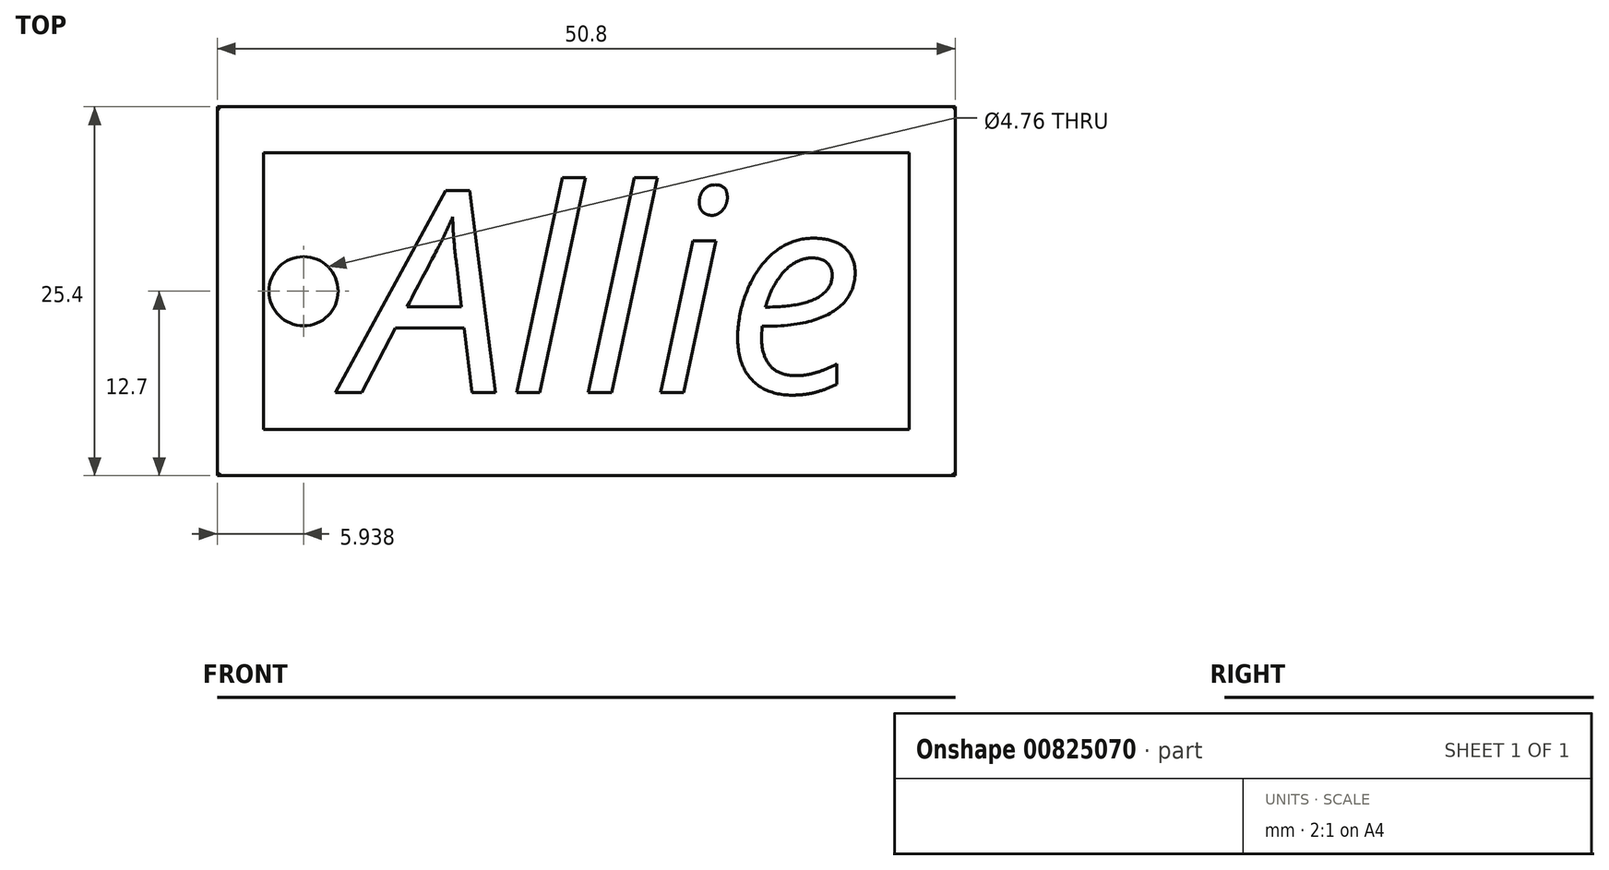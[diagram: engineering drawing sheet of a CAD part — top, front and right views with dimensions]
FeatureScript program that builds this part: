
annotation { "Feature Type Name" : "Feature", "Feature Type Description" : "" }
export const myFeature = defineFeature(function(context is Context, id is Id, definition is map)
    precondition{}
    {
        {
            var Q0;
            Q0=qCreatedBy(makeId("Top.planeOp"),FACE);
            var sketch = newSketch(context, id + "F0", { "sketchPlane" : qUnion([Q0])});
            skLineSegment(sketch, "E0.bottom", {"start": v(0, 0) * mm, "end": v(50.8, 0) * mm});
            skLineSegment(sketch, "E0.top", {"start": v(0, 25.4) * mm, "end": v(50.8, 25.4) * mm});
            skLineSegment(sketch, "E0.left", {"start": v(0, 0) * mm, "end": v(0, 25.4) * mm});
            skLineSegment(sketch, "E0.right", {"start": v(50.8, 0) * mm, "end": v(50.8, 25.4) * mm});
            skCircle(sketch, "E1", {"center": v(5.94, 12.7) * mm, "radius": 2.38 * mm});
            skPoint(sketch, "E1.centerSnap0", {"position": v(0, 12.7) * mm});
            skLineSegment(sketch, "E2.0", {"start": v(3.17, 22.23) * mm, "end": v(47.62, 22.23) * mm});
            skLineSegment(sketch, "E2.1", {"start": v(3.17, 3.18) * mm, "end": v(3.17, 22.23) * mm});
            skLineSegment(sketch, "E2.2", {"start": v(3.17, 3.18) * mm, "end": v(47.62, 3.18) * mm});
            skLineSegment(sketch, "E2.3", {"start": v(47.62, 3.18) * mm, "end": v(47.62, 22.23) * mm});
            skSolve(sketch);
        }
        {
            var Q0;
            Q0=makeQuery(id+"F0.imprint","IMPRINT",FACE,{"disambiguationData":[TD([[makeQuery(id+"F0.imprint","IMPRINT",EDGE,{"derivedFrom":sQuery(id+"F0.wireOp",EDGE,"E1")}),-1.0]])]});
            extrude(context, id + "F1", {"entities" : qUnion([Q0]), "depth" : 1 / 406.4 * mm, "offsetDistance" : 25.4 * mm});
        }
        {
            var Q0;
            Q0 = qSketchRegion(id + "F0", true);
            extrude(context, id + "F2", {"entities" : qUnion([Q0]), "operationType" : NewBodyOperationType.ADD, "depth" : 1 / 203.2 * mm, "offsetDistance" : 25.4 * mm});
        }
        {
            var Q0;
            Q0=makeQuery(id+"F1.opExtrude","CAP_FACE",FACE,{"disambiguationData":[OSD([sQuery(id+"F0.wireOp",EDGE,"E1"),sQuery(id+"F0.wireOp",EDGE,"E2.0"),sQuery(id+"F0.wireOp",EDGE,"E2.1"),sQuery(id+"F0.wireOp",EDGE,"E2.2"),sQuery(id+"F0.wireOp",EDGE,"E2.3")])],"isStart":false});
            var sketch = newSketch(context, id + "F3", { "sketchPlane" : qUnion([Q0])});
            skText(sketch, "E3", { "text": "Allie", "fontName": "OpenSans-Italic.ttf"});
            const initialGuessF3  = {"E3": [0.00925, 0.00574, 1, 0, 0.01402]};
            skSetInitialGuess(sketch, initialGuessF3);
            skSolve(sketch);
        }
        {
            var Q0;
            Q0 = qSketchRegion(id + "F3", true);
            extrude(context, id + "F4", {"entities" : qUnion([Q0]), "operationType" : NewBodyOperationType.ADD, "depth" : 1 / 812.8 * mm, "offsetDistance" : 25.4 * mm});
        }
        {
            var Q0;
            Q0=makeQuery(id+"F2.opExtrude","CAP_EDGE",EDGE,{"disambiguationData":[OSD([sQuery(id+"F0.wireOp",EDGE,"E0.bottom")])],"isStart":false});
            var Q1;
            Q1=makeQuery(id+"F2.opExtrude","CAP_EDGE",EDGE,{"disambiguationData":[OSD([sQuery(id+"F0.wireOp",EDGE,"E0.left")])],"isStart":false});
            var Q2;
            Q2=makeQuery(id+"F2.opExtrude","CAP_EDGE",EDGE,{"disambiguationData":[OSD([sQuery(id+"F0.wireOp",EDGE,"E0.top")])],"isStart":false});
            var Q3;
            Q3=makeQuery(id+"F2.opExtrude","CAP_EDGE",EDGE,{"disambiguationData":[OSD([sQuery(id+"F0.wireOp",EDGE,"E0.right")])],"isStart":false});
            fillet(context, id + "F5", {"entities" : qUnion([Q0, Q1, Q2, Q3]), "radius" : 2.54 * mm, "tangentPropagation" : true, "allowEdgeOverflow" : false});
        }
    });
